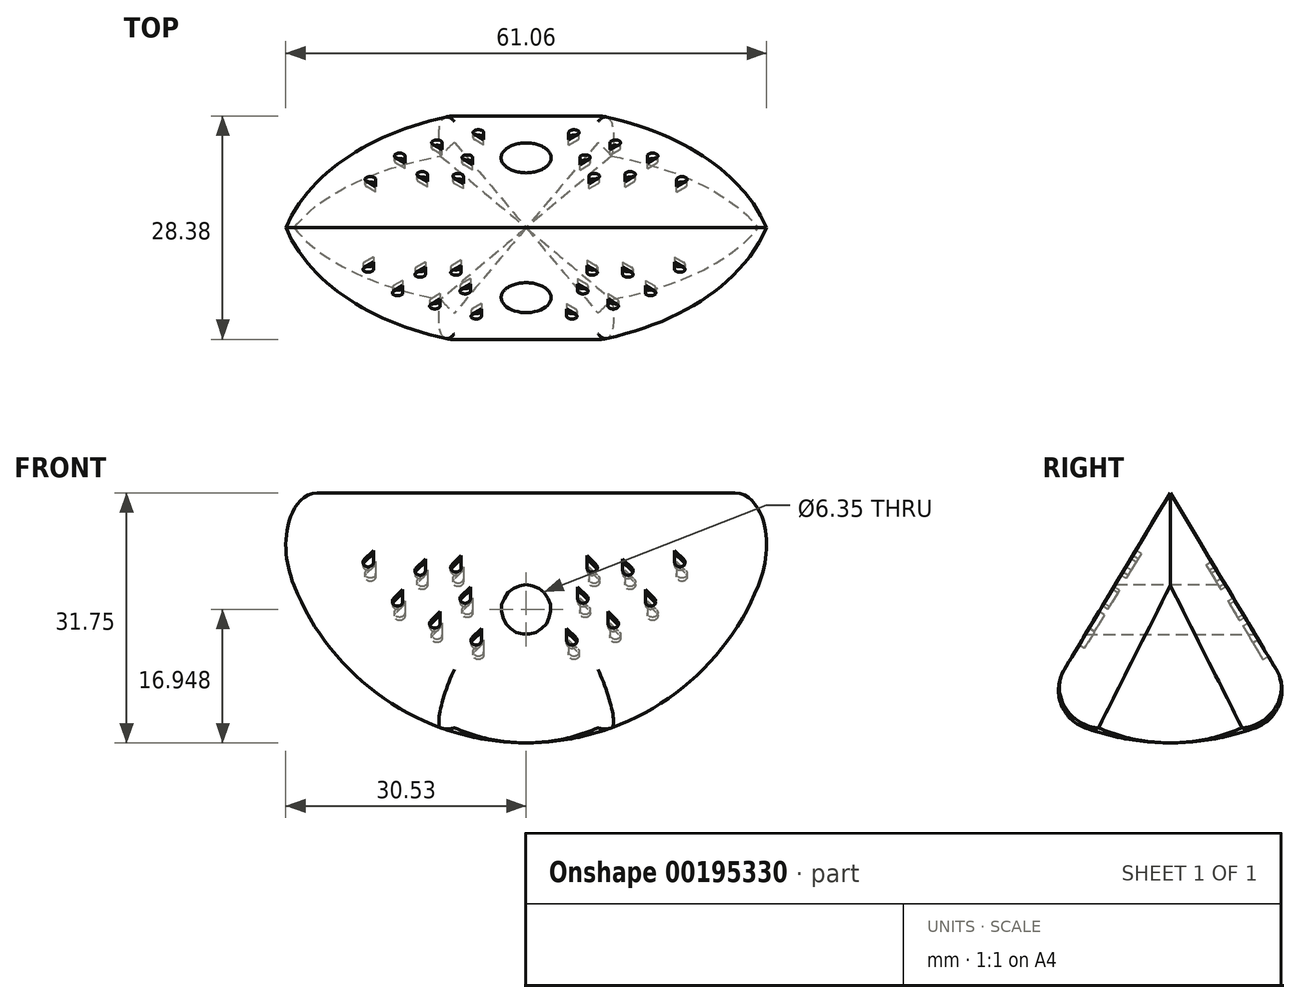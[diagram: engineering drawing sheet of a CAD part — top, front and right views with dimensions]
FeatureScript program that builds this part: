
annotation { "Feature Type Name" : "Feature", "Feature Type Description" : "" }
export const myFeature = defineFeature(function(context is Context, id is Id, definition is map)
    precondition{}
    {
        {
            var Q0;
            Q0=qCreatedBy(makeId("Front.planeOp"),FACE);
            var sketch = newSketch(context, id + "F0", { "sketchPlane" : qUnion([Q0])});
            skLineSegment(sketch, "E0", {"start": v(-31.75, 0) * mm, "end": v(31.75, 0) * mm});
            skArc(sketch, "E1", {"start": v(31.75, 0) * mm, "mid": v(0, -31.75) * mm, "end": v(-31.75, 0) * mm});
            skSolve(sketch);
        }
        {
            var Q0;
            Q0 = qSketchRegion(id + "F0", true);
            extrude(context, id + "F1", {"entities" : qUnion([Q0]), "endBound" : BoundingType.SYMMETRIC, "depth" : 38.1 * mm});
        }
        {
            var Q0;
            Q0=qCreatedBy(makeId("Right.planeOp"),FACE);
            var sketch = newSketch(context, id + "F2", { "sketchPlane" : qUnion([Q0])});
            skLineSegment(sketch, "E2", {"start": v(0, 0) * mm, "end": v(19.05, -31.75) * mm});
            skLineSegment(sketch, "E3", {"start": v(19.05, -31.75) * mm, "end": v(19.05, 0) * mm});
            skLineSegment(sketch, "E4", {"start": v(0, 0) * mm, "end": v(19.05, 0) * mm});
            skLineSegment(sketch, "E5", {"start": v(0, 0) * mm, "end": v(0, -31.88) * mm, "construction": true});
            skLineSegment(sketch, "E6.MirrorCS", {"start": v(-19.05, -31.75) * mm, "end": v(-19.05, 0) * mm});
            skLineSegment(sketch, "E7.MirrorCS", {"start": v(0, 0) * mm, "end": v(-19.05, 0) * mm});
            skLineSegment(sketch, "E8.MirrorCS", {"start": v(0, 0) * mm, "end": v(-19.05, -31.75) * mm});
            skSolve(sketch);
        }
        {
            var Q0;
            Q0 = qSketchRegion(id + "F2", true);
            extrude(context, id + "F3", {"entities" : qUnion([Q0]), "operationType" : NewBodyOperationType.REMOVE, "endBound" : BoundingType.SYMMETRIC, "depth" : 76.2 * mm});
        }
        {
            var Q0;
            Q0=qCreatedBy(makeId("Right.planeOp"),FACE);
            var sketch = newSketch(context, id + "F4", { "sketchPlane" : qUnion([Q0])});
            skArc(sketch, "E9", {"start": v(-31.75, 0) * mm, "mid": v(0, -31.75) * mm, "end": v(31.75, 0) * mm});
            skLineSegment(sketch, "E10", {"start": v(31.75, 0) * mm, "end": v(31.75, -50.8) * mm});
            skLineSegment(sketch, "E11", {"start": v(31.75, -50.8) * mm, "end": v(-31.75, -50.8) * mm});
            skLineSegment(sketch, "E12", {"start": v(-31.75, -50.8) * mm, "end": v(-31.75, 0) * mm});
            skSolve(sketch);
        }
        {
            var Q0;
            Q0 = qSketchRegion(id + "F4", true);
            extrude(context, id + "F5", {"entities" : qUnion([Q0]), "operationType" : NewBodyOperationType.REMOVE, "endBound" : BoundingType.SYMMETRIC, "oppositeDirection" : true, "depth" : 127 * mm});
        }
        {
            var Q0;
            Q0=makeQuery(id+"F5.boolean.opBoolean","INTERSECT",EDGE,{"disambiguationData":[OD(2.0)],"derivedFrom":[makeQuery(id+"F1.opExtrude","SWEPT_FACE",FACE,{"disambiguationData":[OSD([sQuery(id+"F0.wireOp",EDGE,"E1")])]}),makeQuery(id+"F5.opExtrude","SWEPT_FACE",FACE,{"disambiguationData":[OSD([sQuery(id+"F4.wireOp",EDGE,"E9")])]})]});
            var Q1;
            Q1=makeQuery(id+"F5.boolean.opBoolean","INTERSECT",EDGE,{"disambiguationData":[OD(3.0)],"derivedFrom":[makeQuery(id+"F1.opExtrude","SWEPT_FACE",FACE,{"disambiguationData":[OSD([sQuery(id+"F0.wireOp",EDGE,"E1")])]}),makeQuery(id+"F5.opExtrude","SWEPT_FACE",FACE,{"disambiguationData":[OSD([sQuery(id+"F4.wireOp",EDGE,"E9")])]})]});
            var Q2;
            Q2=makeQuery(id+"F5.boolean.opBoolean","INTERSECT",EDGE,{"disambiguationData":[OD(1.0)],"derivedFrom":[makeQuery(id+"F1.opExtrude","SWEPT_FACE",FACE,{"disambiguationData":[OSD([sQuery(id+"F0.wireOp",EDGE,"E1")])]}),makeQuery(id+"F5.opExtrude","SWEPT_FACE",FACE,{"disambiguationData":[OSD([sQuery(id+"F4.wireOp",EDGE,"E9")])]})]});
            var Q3;
            Q3=makeQuery(id+"F5.boolean.opBoolean","INTERSECT",EDGE,{"disambiguationData":[OD(0.0)],"derivedFrom":[makeQuery(id+"F1.opExtrude","SWEPT_FACE",FACE,{"disambiguationData":[OSD([sQuery(id+"F0.wireOp",EDGE,"E1")])]}),makeQuery(id+"F5.opExtrude","SWEPT_FACE",FACE,{"disambiguationData":[OSD([sQuery(id+"F4.wireOp",EDGE,"E9")])]})]});
            var Q4;
            Q4=makeQuery(id+"F5.boolean.opBoolean","SPLIT",EDGE,{"disambiguationData":[OD(0.0)],"derivedFrom":makeQuery(id+"F3.boolean.opBoolean","INTERSECT",EDGE,{"derivedFrom":[makeQuery(id+"F1.opExtrude","SWEPT_FACE",FACE,{"disambiguationData":[OSD([sQuery(id+"F0.wireOp",EDGE,"E1")])]}),makeQuery(id+"F3.opExtrude","SWEPT_FACE",FACE,{"disambiguationData":[OSD([sQuery(id+"F2.wireOp",EDGE,"E8.MirrorCS")])]})]})});
            var Q5;
            Q5=makeQuery(id+"F5.boolean.opBoolean","INTERSECT",EDGE,{"derivedFrom":[makeQuery(id+"F3.boolean.opBoolean","COPY",FACE,{"derivedFrom":makeQuery(id+"F3.opExtrude","SWEPT_FACE",FACE,{"disambiguationData":[OSD([sQuery(id+"F2.wireOp",EDGE,"E8.MirrorCS")])]})}),makeQuery(id+"F5.opExtrude","SWEPT_FACE",FACE,{"disambiguationData":[OSD([sQuery(id+"F4.wireOp",EDGE,"E9")])]})]});
            var Q6;
            Q6=makeQuery(id+"F5.boolean.opBoolean","SPLIT",EDGE,{"disambiguationData":[OD(1.0)],"derivedFrom":makeQuery(id+"F3.boolean.opBoolean","INTERSECT",EDGE,{"derivedFrom":[makeQuery(id+"F1.opExtrude","SWEPT_FACE",FACE,{"disambiguationData":[OSD([sQuery(id+"F0.wireOp",EDGE,"E1")])]}),makeQuery(id+"F3.opExtrude","SWEPT_FACE",FACE,{"disambiguationData":[OSD([sQuery(id+"F2.wireOp",EDGE,"E8.MirrorCS")])]})]})});
            var Q7;
            {var subQ0=sQuery(id+"F2.wireOp",EDGE,"E8.MirrorCS");var subQ1=sQuery(id+"F2.wireOp",EDGE,"E7.MirrorCS");var subQ2=sQuery(id+"F2.wireOp",EDGE,"E4");var subQ3=sQuery(id+"F2.wireOp",EDGE,"E2");Q7=makeQuery(id+"F3.boolean.opBoolean","TWEAK_EDGE",EDGE,{"derivedFrom":[makeQuery(id+"F3.opExtrude","SWEPT_EDGE",EDGE,{"disambiguationData":[OSD([subQ3,subQ2,subQ1,subQ0]),ownerDisambiguation([makeQuery(id+"F3.opExtrude","SWEPT_BODY",BODY,{"disambiguationData":[OSD([subQ3,sQuery(id+"F2.wireOp",EDGE,"E3"),subQ2])]})])]}),makeQuery(id+"F3.opExtrude","SWEPT_EDGE",EDGE,{"disambiguationData":[OSD([subQ3,subQ2,subQ1,subQ0]),ownerDisambiguation([makeQuery(id+"F3.opExtrude","SWEPT_BODY",BODY,{"disambiguationData":[OSD([subQ1,subQ0,sQuery(id+"F2.wireOp",EDGE,"E6.MirrorCS")])]})])]})]});}
            var Q8;
            Q8=makeQuery(id+"F5.boolean.opBoolean","SPLIT",EDGE,{"disambiguationData":[OD(0.0)],"derivedFrom":makeQuery(id+"F3.boolean.opBoolean","INTERSECT",EDGE,{"derivedFrom":[makeQuery(id+"F1.opExtrude","SWEPT_FACE",FACE,{"disambiguationData":[OSD([sQuery(id+"F0.wireOp",EDGE,"E1")])]}),makeQuery(id+"F3.opExtrude","SWEPT_FACE",FACE,{"disambiguationData":[OSD([sQuery(id+"F2.wireOp",EDGE,"E2")])]})]})});
            var Q9;
            Q9=makeQuery(id+"F5.boolean.opBoolean","INTERSECT",EDGE,{"derivedFrom":[makeQuery(id+"F3.boolean.opBoolean","COPY",FACE,{"derivedFrom":makeQuery(id+"F3.opExtrude","SWEPT_FACE",FACE,{"disambiguationData":[OSD([sQuery(id+"F2.wireOp",EDGE,"E2")])]})}),makeQuery(id+"F5.opExtrude","SWEPT_FACE",FACE,{"disambiguationData":[OSD([sQuery(id+"F4.wireOp",EDGE,"E9")])]})]});
            var Q10;
            Q10=makeQuery(id+"F5.boolean.opBoolean","SPLIT",EDGE,{"disambiguationData":[OD(1.0)],"derivedFrom":makeQuery(id+"F3.boolean.opBoolean","INTERSECT",EDGE,{"derivedFrom":[makeQuery(id+"F1.opExtrude","SWEPT_FACE",FACE,{"disambiguationData":[OSD([sQuery(id+"F0.wireOp",EDGE,"E1")])]}),makeQuery(id+"F3.opExtrude","SWEPT_FACE",FACE,{"disambiguationData":[OSD([sQuery(id+"F2.wireOp",EDGE,"E2")])]})]})});
            fillet(context, id + "F6", {"entities" : qUnion([Q0, Q1, Q2, Q3, Q4, Q5, Q6, Q7, Q8, Q9, Q10]), "radius" : 5.08 * mm, "tangentPropagation" : true, "allowEdgeOverflow" : false});
        }
        {
            var Q0;
            Q0=qCreatedBy(makeId("Front.planeOp"),FACE);
            var sketch = newSketch(context, id + "F7", { "sketchPlane" : qUnion([Q0])});
            skCircle(sketch, "E13", {"center": v(0, -14.8) * mm, "radius": 3.17 * mm});
            skSolve(sketch);
        }
        {
            var Q0;
            Q0 = qSketchRegion(id + "F7", true);
            extrude(context, id + "F8", {"entities" : qUnion([Q0]), "operationType" : NewBodyOperationType.REMOVE, "endBound" : BoundingType.SYMMETRIC, "depth" : 127 * mm});
        }
        {
            var Q0;
            Q0=makeQuery(id+"F3.boolean.opBoolean","COPY",FACE,{"derivedFrom":makeQuery(id+"F3.opExtrude","SWEPT_FACE",FACE,{"disambiguationData":[OSD([sQuery(id+"F2.wireOp",EDGE,"E2")])]})});
            var sketch = newSketch(context, id + "F9", { "sketchPlane" : qUnion([Q0])});
            skLineSegment(sketch, "E14", {"start": v(-19.13, -10.17) * mm, "end": v(-20.3, -11.52) * mm});
            skLineSegment(sketch, "E15", {"start": v(-19.13, -10.17) * mm, "end": v(-19.13, -11.95) * mm});
            skArc(sketch, "E16", {"start": v(-20.3, -11.52) * mm, "mid": v(-20.03, -12.58) * mm, "end": v(-19.13, -11.95) * mm});
            skLineSegment(sketch, "E17", {"start": v(-15.4, -15.97) * mm, "end": v(-16.57, -17.31) * mm});
            skLineSegment(sketch, "E18", {"start": v(-15.4, -15.97) * mm, "end": v(-15.4, -17.75) * mm});
            skArc(sketch, "E19", {"start": v(-16.57, -17.31) * mm, "mid": v(-16.3, -18.37) * mm, "end": v(-15.4, -17.75) * mm});
            skLineSegment(sketch, "E20", {"start": v(-10.67, -19.24) * mm, "end": v(-11.84, -20.58) * mm});
            skLineSegment(sketch, "E21", {"start": v(-10.67, -19.24) * mm, "end": v(-10.67, -21.02) * mm});
            skArc(sketch, "E22", {"start": v(-11.84, -20.58) * mm, "mid": v(-11.57, -21.64) * mm, "end": v(-10.67, -21.02) * mm});
            skLineSegment(sketch, "E23", {"start": v(-5.41, -21.75) * mm, "end": v(-6.58, -23.1) * mm});
            skLineSegment(sketch, "E24", {"start": v(-5.41, -21.75) * mm, "end": v(-5.41, -23.53) * mm});
            skArc(sketch, "E25", {"start": v(-6.58, -23.1) * mm, "mid": v(-6.3, -24.16) * mm, "end": v(-5.41, -23.53) * mm});
            skLineSegment(sketch, "E26", {"start": v(-6.81, -15.56) * mm, "end": v(-7.98, -16.9) * mm});
            skLineSegment(sketch, "E27", {"start": v(-6.81, -15.56) * mm, "end": v(-6.81, -17.34) * mm});
            skArc(sketch, "E28", {"start": v(-7.98, -16.9) * mm, "mid": v(-7.71, -17.96) * mm, "end": v(-6.81, -17.34) * mm});
            skLineSegment(sketch, "E29", {"start": v(-12.54, -11.41) * mm, "end": v(-13.7, -12.75) * mm});
            skLineSegment(sketch, "E30", {"start": v(-12.54, -11.41) * mm, "end": v(-12.54, -13.2) * mm});
            skArc(sketch, "E31", {"start": v(-13.7, -12.75) * mm, "mid": v(-13.44, -13.82) * mm, "end": v(-12.54, -13.2) * mm});
            skLineSegment(sketch, "E32", {"start": v(-7.98, -10.94) * mm, "end": v(-9.15, -12.29) * mm});
            skLineSegment(sketch, "E33", {"start": v(-7.98, -10.94) * mm, "end": v(-7.98, -12.72) * mm});
            skArc(sketch, "E34", {"start": v(-9.15, -12.29) * mm, "mid": v(-8.88, -13.35) * mm, "end": v(-7.98, -12.72) * mm});
            skLineSegment(sketch, "E35.MirrorCS", {"start": v(6.81, -15.56) * mm, "end": v(7.98, -16.9) * mm});
            skLineSegment(sketch, "E36.MirrorCS", {"start": v(19.13, -10.17) * mm, "end": v(20.3, -11.52) * mm});
            skLineSegment(sketch, "E37.MirrorCS", {"start": v(12.54, -11.41) * mm, "end": v(13.7, -12.75) * mm});
            skArc(sketch, "E38.MirrorCS", {"start": v(16.57, -17.31) * mm, "mid": v(16.3, -18.37) * mm, "end": v(15.4, -17.75) * mm});
            skArc(sketch, "E39.MirrorCS", {"start": v(13.7, -12.75) * mm, "mid": v(13.44, -13.82) * mm, "end": v(12.54, -13.2) * mm});
            skLineSegment(sketch, "E40.MirrorCS", {"start": v(19.13, -10.17) * mm, "end": v(19.13, -11.95) * mm});
            skArc(sketch, "E41.MirrorCS", {"start": v(6.58, -23.1) * mm, "mid": v(6.3, -24.16) * mm, "end": v(5.41, -23.53) * mm});
            skLineSegment(sketch, "E42.MirrorCS", {"start": v(10.67, -19.24) * mm, "end": v(11.84, -20.58) * mm});
            skLineSegment(sketch, "E43.MirrorCS", {"start": v(5.41, -21.75) * mm, "end": v(5.41, -23.53) * mm});
            skArc(sketch, "E44.MirrorCS", {"start": v(20.3, -11.52) * mm, "mid": v(20.03, -12.58) * mm, "end": v(19.13, -11.95) * mm});
            skLineSegment(sketch, "E45.MirrorCS", {"start": v(10.67, -19.24) * mm, "end": v(10.67, -21.02) * mm});
            skLineSegment(sketch, "E46.MirrorCS", {"start": v(15.4, -15.97) * mm, "end": v(16.57, -17.31) * mm});
            skArc(sketch, "E47.MirrorCS", {"start": v(7.98, -16.9) * mm, "mid": v(7.71, -17.96) * mm, "end": v(6.81, -17.34) * mm});
            skLineSegment(sketch, "E48.MirrorCS", {"start": v(5.41, -21.75) * mm, "end": v(6.58, -23.1) * mm});
            skArc(sketch, "E49.MirrorCS", {"start": v(11.84, -20.58) * mm, "mid": v(11.57, -21.64) * mm, "end": v(10.67, -21.02) * mm});
            skLineSegment(sketch, "E50.MirrorCS", {"start": v(6.81, -15.56) * mm, "end": v(6.81, -17.34) * mm});
            skLineSegment(sketch, "E51.MirrorCS", {"start": v(15.4, -15.97) * mm, "end": v(15.4, -17.75) * mm});
            skLineSegment(sketch, "E52.MirrorCS", {"start": v(12.54, -11.41) * mm, "end": v(12.54, -13.2) * mm});
            skArc(sketch, "E53.MirrorCS", {"start": v(9.15, -12.29) * mm, "mid": v(8.88, -13.35) * mm, "end": v(7.98, -12.72) * mm});
            skLineSegment(sketch, "E54.MirrorCS", {"start": v(7.98, -10.94) * mm, "end": v(9.15, -12.29) * mm});
            skLineSegment(sketch, "E55.MirrorCS", {"start": v(7.98, -10.94) * mm, "end": v(7.98, -12.72) * mm});
            skSolve(sketch);
        }
        {
            var Q0;
            Q0 = qSketchRegion(id + "F9", true);
            extrude(context, id + "F10", {"entities" : qUnion([Q0]), "operationType" : NewBodyOperationType.REMOVE, "oppositeDirection" : true, "depth" : 0.8 * mm});
        }
        {
            var Q0;
            Q0=makeQuery(id+"F3.boolean.opBoolean","COPY",FACE,{"derivedFrom":makeQuery(id+"F3.opExtrude","SWEPT_FACE",FACE,{"disambiguationData":[OSD([sQuery(id+"F2.wireOp",EDGE,"E8.MirrorCS")])]})});
            var sketch = newSketch(context, id + "F11", { "sketchPlane" : qUnion([Q0])});
            skLineSegment(sketch, "E56", {"start": v(-19.4, -8.51) * mm, "end": v(-20.56, -9.86) * mm});
            skLineSegment(sketch, "E57", {"start": v(-19.4, -8.51) * mm, "end": v(-19.4, -10.3) * mm});
            skArc(sketch, "E58", {"start": v(-20.56, -9.86) * mm, "mid": v(-20.3, -10.92) * mm, "end": v(-19.4, -10.3) * mm});
            skLineSegment(sketch, "E59", {"start": v(-15.67, -14.3) * mm, "end": v(-16.84, -15.65) * mm});
            skLineSegment(sketch, "E60", {"start": v(-15.67, -14.3) * mm, "end": v(-15.67, -16.09) * mm});
            skArc(sketch, "E61", {"start": v(-16.84, -15.65) * mm, "mid": v(-16.57, -16.71) * mm, "end": v(-15.67, -16.09) * mm});
            skLineSegment(sketch, "E62", {"start": v(-10.94, -17.58) * mm, "end": v(-12.1, -18.92) * mm});
            skLineSegment(sketch, "E63", {"start": v(-10.94, -17.58) * mm, "end": v(-10.94, -19.36) * mm});
            skArc(sketch, "E64", {"start": v(-12.1, -18.92) * mm, "mid": v(-11.84, -19.98) * mm, "end": v(-10.94, -19.36) * mm});
            skLineSegment(sketch, "E65", {"start": v(-5.68, -20.1) * mm, "end": v(-6.85, -21.43) * mm});
            skLineSegment(sketch, "E66", {"start": v(-5.68, -20.1) * mm, "end": v(-5.68, -21.87) * mm});
            skArc(sketch, "E67", {"start": v(-6.85, -21.43) * mm, "mid": v(-6.58, -22.5) * mm, "end": v(-5.68, -21.87) * mm});
            skLineSegment(sketch, "E68", {"start": v(-7.08, -13.9) * mm, "end": v(-8.25, -15.24) * mm});
            skLineSegment(sketch, "E69", {"start": v(-7.08, -13.9) * mm, "end": v(-7.08, -15.68) * mm});
            skArc(sketch, "E70", {"start": v(-8.25, -15.24) * mm, "mid": v(-7.98, -16.3) * mm, "end": v(-7.08, -15.68) * mm});
            skLineSegment(sketch, "E71", {"start": v(-12.8, -9.75) * mm, "end": v(-13.98, -11.1) * mm});
            skLineSegment(sketch, "E72", {"start": v(-12.8, -9.75) * mm, "end": v(-12.8, -11.53) * mm});
            skArc(sketch, "E73", {"start": v(-13.98, -11.1) * mm, "mid": v(-13.7, -12.15) * mm, "end": v(-12.8, -11.53) * mm});
            skLineSegment(sketch, "E74", {"start": v(-8.25, -9.28) * mm, "end": v(-9.42, -10.63) * mm});
            skLineSegment(sketch, "E75", {"start": v(-8.25, -9.28) * mm, "end": v(-8.25, -11.06) * mm});
            skArc(sketch, "E76", {"start": v(-9.42, -10.63) * mm, "mid": v(-9.15, -11.69) * mm, "end": v(-8.25, -11.06) * mm});
            skLineSegment(sketch, "E77.MirrorCS", {"start": v(6.54, -13.9) * mm, "end": v(7.71, -15.24) * mm});
            skLineSegment(sketch, "E78.MirrorCS", {"start": v(18.86, -8.51) * mm, "end": v(20.03, -9.86) * mm});
            skLineSegment(sketch, "E79.MirrorCS", {"start": v(12.27, -9.75) * mm, "end": v(13.44, -11.1) * mm});
            skArc(sketch, "E80.MirrorCS", {"start": v(16.3, -15.65) * mm, "mid": v(16.03, -16.71) * mm, "end": v(15.13, -16.09) * mm});
            skArc(sketch, "E81.MirrorCS", {"start": v(13.44, -11.1) * mm, "mid": v(13.17, -12.15) * mm, "end": v(12.27, -11.53) * mm});
            skLineSegment(sketch, "E82.MirrorCS", {"start": v(18.86, -8.51) * mm, "end": v(18.86, -10.3) * mm});
            skArc(sketch, "E83.MirrorCS", {"start": v(6.3, -21.43) * mm, "mid": v(6.04, -22.5) * mm, "end": v(5.14, -21.87) * mm});
            skLineSegment(sketch, "E84.MirrorCS", {"start": v(10.4, -17.58) * mm, "end": v(11.57, -18.92) * mm});
            skLineSegment(sketch, "E85.MirrorCS", {"start": v(5.14, -20.1) * mm, "end": v(5.14, -21.87) * mm});
            skArc(sketch, "E86.MirrorCS", {"start": v(20.03, -9.86) * mm, "mid": v(19.76, -10.92) * mm, "end": v(18.86, -10.3) * mm});
            skLineSegment(sketch, "E87.MirrorCS", {"start": v(10.4, -17.58) * mm, "end": v(10.4, -19.36) * mm});
            skLineSegment(sketch, "E88.MirrorCS", {"start": v(15.13, -14.3) * mm, "end": v(16.3, -15.65) * mm});
            skArc(sketch, "E89.MirrorCS", {"start": v(7.71, -15.24) * mm, "mid": v(7.44, -16.3) * mm, "end": v(6.54, -15.68) * mm});
            skLineSegment(sketch, "E90.MirrorCS", {"start": v(5.14, -20.1) * mm, "end": v(6.3, -21.43) * mm});
            skArc(sketch, "E91.MirrorCS", {"start": v(11.57, -18.92) * mm, "mid": v(11.3, -19.98) * mm, "end": v(10.4, -19.36) * mm});
            skLineSegment(sketch, "E92.MirrorCS", {"start": v(6.54, -13.9) * mm, "end": v(6.54, -15.68) * mm});
            skLineSegment(sketch, "E93.MirrorCS", {"start": v(15.13, -14.3) * mm, "end": v(15.13, -16.09) * mm});
            skLineSegment(sketch, "E94.MirrorCS", {"start": v(12.27, -9.75) * mm, "end": v(12.27, -11.53) * mm});
            skArc(sketch, "E95.MirrorCS", {"start": v(8.88, -10.63) * mm, "mid": v(8.61, -11.69) * mm, "end": v(7.71, -11.06) * mm});
            skLineSegment(sketch, "E96.MirrorCS", {"start": v(7.71, -9.28) * mm, "end": v(8.88, -10.63) * mm});
            skLineSegment(sketch, "E97.MirrorCS", {"start": v(7.71, -9.28) * mm, "end": v(7.71, -11.06) * mm});
            skSolve(sketch);
        }
        {
            var Q0;
            Q0 = qSketchRegion(id + "F11", true);
            var Q1;
            Q1=sQuery(id+"F11.wireOp",EDGE,"E56");
            var Q2;
            Q2=sQuery(id+"F11.wireOp",EDGE,"E57");
            var Q3;
            Q3=sQuery(id+"F11.wireOp",EDGE,"E58");
            var Q4;
            Q4=sQuery(id+"F11.wireOp",EDGE,"E59");
            var Q5;
            Q5=sQuery(id+"F11.wireOp",EDGE,"E60");
            var Q6;
            Q6=sQuery(id+"F11.wireOp",EDGE,"E61");
            var Q7;
            Q7=sQuery(id+"F11.wireOp",EDGE,"E62");
            var Q8;
            Q8=sQuery(id+"F11.wireOp",EDGE,"E63");
            var Q9;
            Q9=sQuery(id+"F11.wireOp",EDGE,"E64");
            var Q10;
            Q10=sQuery(id+"F11.wireOp",EDGE,"E65");
            var Q11;
            Q11=sQuery(id+"F11.wireOp",EDGE,"E66");
            var Q12;
            Q12=sQuery(id+"F11.wireOp",EDGE,"E67");
            var Q13;
            Q13=sQuery(id+"F11.wireOp",EDGE,"E68");
            var Q14;
            Q14=sQuery(id+"F11.wireOp",EDGE,"E69");
            var Q15;
            Q15=sQuery(id+"F11.wireOp",EDGE,"E70");
            var Q16;
            Q16=sQuery(id+"F11.wireOp",EDGE,"E71");
            var Q17;
            Q17=sQuery(id+"F11.wireOp",EDGE,"E72");
            var Q18;
            Q18=sQuery(id+"F11.wireOp",EDGE,"E73");
            var Q19;
            Q19=sQuery(id+"F11.wireOp",EDGE,"E74");
            var Q20;
            Q20=sQuery(id+"F11.wireOp",EDGE,"E75");
            var Q21;
            Q21=sQuery(id+"F11.wireOp",EDGE,"E76");
            var Q22;
            Q22=sQuery(id+"F11.wireOp",EDGE,"E77.MirrorCS");
            var Q23;
            Q23=sQuery(id+"F11.wireOp",EDGE,"E78.MirrorCS");
            var Q24;
            Q24=sQuery(id+"F11.wireOp",EDGE,"E79.MirrorCS");
            var Q25;
            Q25=sQuery(id+"F11.wireOp",EDGE,"E80.MirrorCS");
            var Q26;
            Q26=sQuery(id+"F11.wireOp",EDGE,"E81.MirrorCS");
            var Q27;
            Q27=sQuery(id+"F11.wireOp",EDGE,"E82.MirrorCS");
            var Q28;
            Q28=sQuery(id+"F11.wireOp",EDGE,"E83.MirrorCS");
            var Q29;
            Q29=sQuery(id+"F11.wireOp",EDGE,"E84.MirrorCS");
            var Q30;
            Q30=sQuery(id+"F11.wireOp",EDGE,"E85.MirrorCS");
            var Q31;
            Q31=sQuery(id+"F11.wireOp",EDGE,"E86.MirrorCS");
            var Q32;
            Q32=sQuery(id+"F11.wireOp",EDGE,"E87.MirrorCS");
            var Q33;
            Q33=sQuery(id+"F11.wireOp",EDGE,"E88.MirrorCS");
            var Q34;
            Q34=sQuery(id+"F11.wireOp",EDGE,"E89.MirrorCS");
            var Q35;
            Q35=sQuery(id+"F11.wireOp",EDGE,"E90.MirrorCS");
            var Q36;
            Q36=sQuery(id+"F11.wireOp",EDGE,"E91.MirrorCS");
            var Q37;
            Q37=sQuery(id+"F11.wireOp",EDGE,"E92.MirrorCS");
            var Q38;
            Q38=sQuery(id+"F11.wireOp",EDGE,"E93.MirrorCS");
            var Q39;
            Q39=sQuery(id+"F11.wireOp",EDGE,"E94.MirrorCS");
            var Q40;
            Q40=sQuery(id+"F11.wireOp",EDGE,"E95.MirrorCS");
            var Q41;
            Q41=sQuery(id+"F11.wireOp",EDGE,"E96.MirrorCS");
            var Q42;
            Q42=sQuery(id+"F11.wireOp",EDGE,"E97.MirrorCS");
            extrude(context, id + "F12", {"entities" : qUnion([Q0]), "operationType" : NewBodyOperationType.REMOVE, "surfaceEntities" : qUnion([Q1, Q2, Q3, Q4, Q5, Q6, Q7, Q8, Q9, Q10, Q11, Q12, Q13, Q14, Q15, Q16, Q17, Q18, Q19, Q20, Q21, Q22, Q23, Q24, Q25, Q26, Q27, Q28, Q29, Q30, Q31, Q32, Q33, Q34, Q35, Q36, Q37, Q38, Q39, Q40, Q41, Q42]), "oppositeDirection" : true, "depth" : 0.8 * mm});
        }
    });
